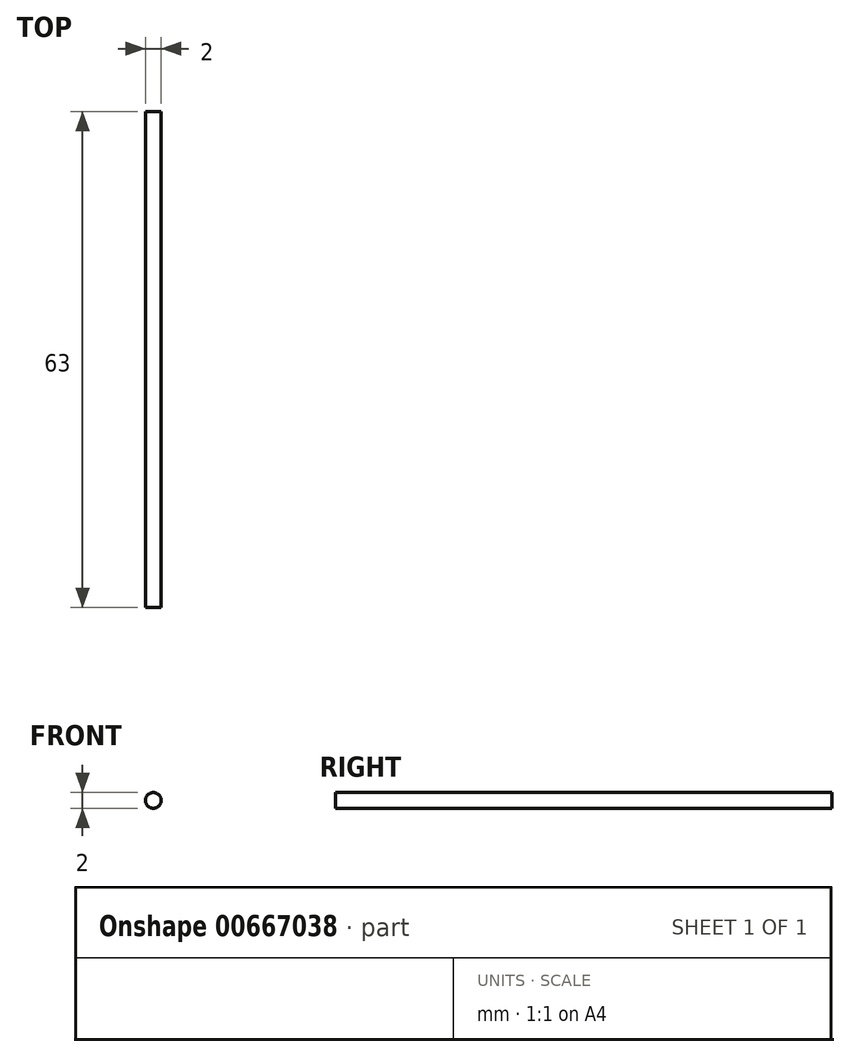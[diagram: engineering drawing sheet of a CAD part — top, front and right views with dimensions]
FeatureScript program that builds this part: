
annotation { "Feature Type Name" : "Feature", "Feature Type Description" : "" }
export const myFeature = defineFeature(function(context is Context, id is Id, definition is map)
    precondition{}
    {
        {
            var Q0;
            Q0=qCreatedBy(makeId("Front.planeOp"),FACE);
            var sketch = newSketch(context, id + "F0", { "sketchPlane" : qUnion([Q0])});
            skCircle(sketch, "E0", {"center": v(12.2, 15.62) * mm, "radius": 1 * mm});
            skSolve(sketch);
        }
        {
            var Q0;
            Q0=makeQuery(id+"F0.imprint","IMPRINT",FACE,{"disambiguationData":[TD([[makeQuery(id+"F0.imprint","IMPRINT",EDGE,{"derivedFrom":sQuery(id+"F0.wireOp",EDGE,"E0")}),1.0]])]});
            extrude(context, id + "F1", {"entities" : qUnion([Q0]), "oppositeDirection" : true, "depth" : 63 * mm, "offsetDistance" : 25.4 * mm});
        }
    });
